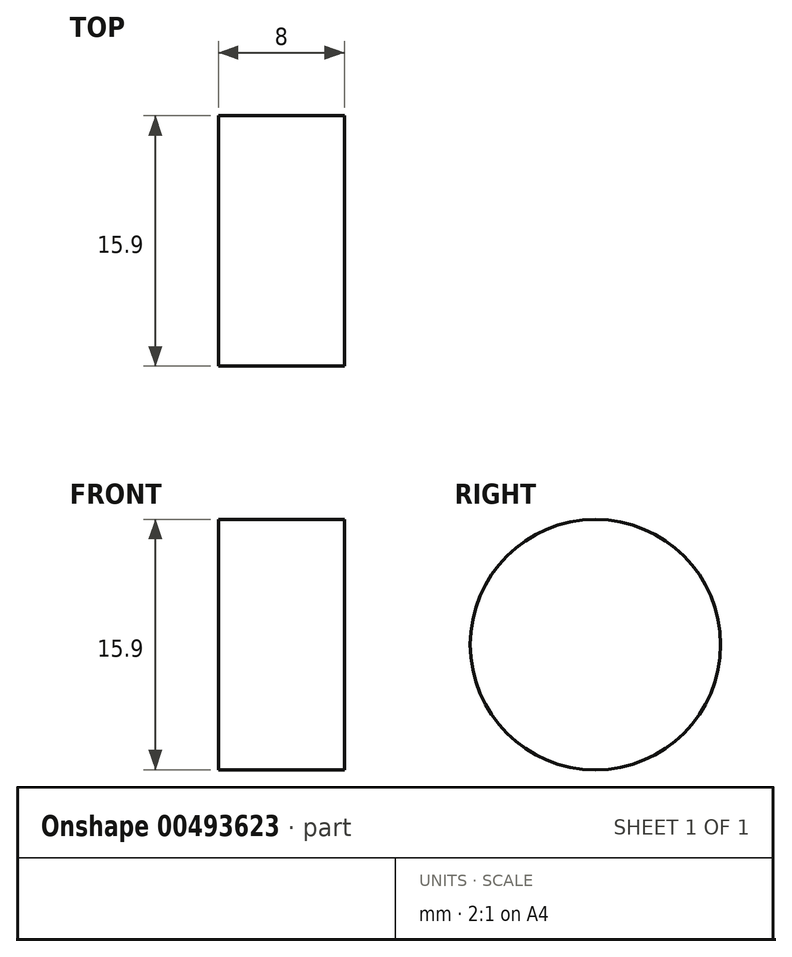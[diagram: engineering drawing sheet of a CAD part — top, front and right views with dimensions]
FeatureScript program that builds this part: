
annotation { "Feature Type Name" : "Feature", "Feature Type Description" : "" }
export const myFeature = defineFeature(function(context is Context, id is Id, definition is map)
    precondition{}
    {
        {
            var Q0;
            Q0=qCreatedBy(makeId("Right.planeOp"),FACE);
            var sketch = newSketch(context, id + "F0", { "sketchPlane" : qUnion([Q0])});
            skCircle(sketch, "E0", {"center": v(0, 0) * mm, "radius": 7.95 * mm});
            skSolve(sketch);
        }
        {
            var Q0;
            Q0 = qSketchRegion(id + "F0", true);
            extrude(context, id + "F1", {"entities" : qUnion([Q0]), "depth" : 8 * mm});
        }
    });
